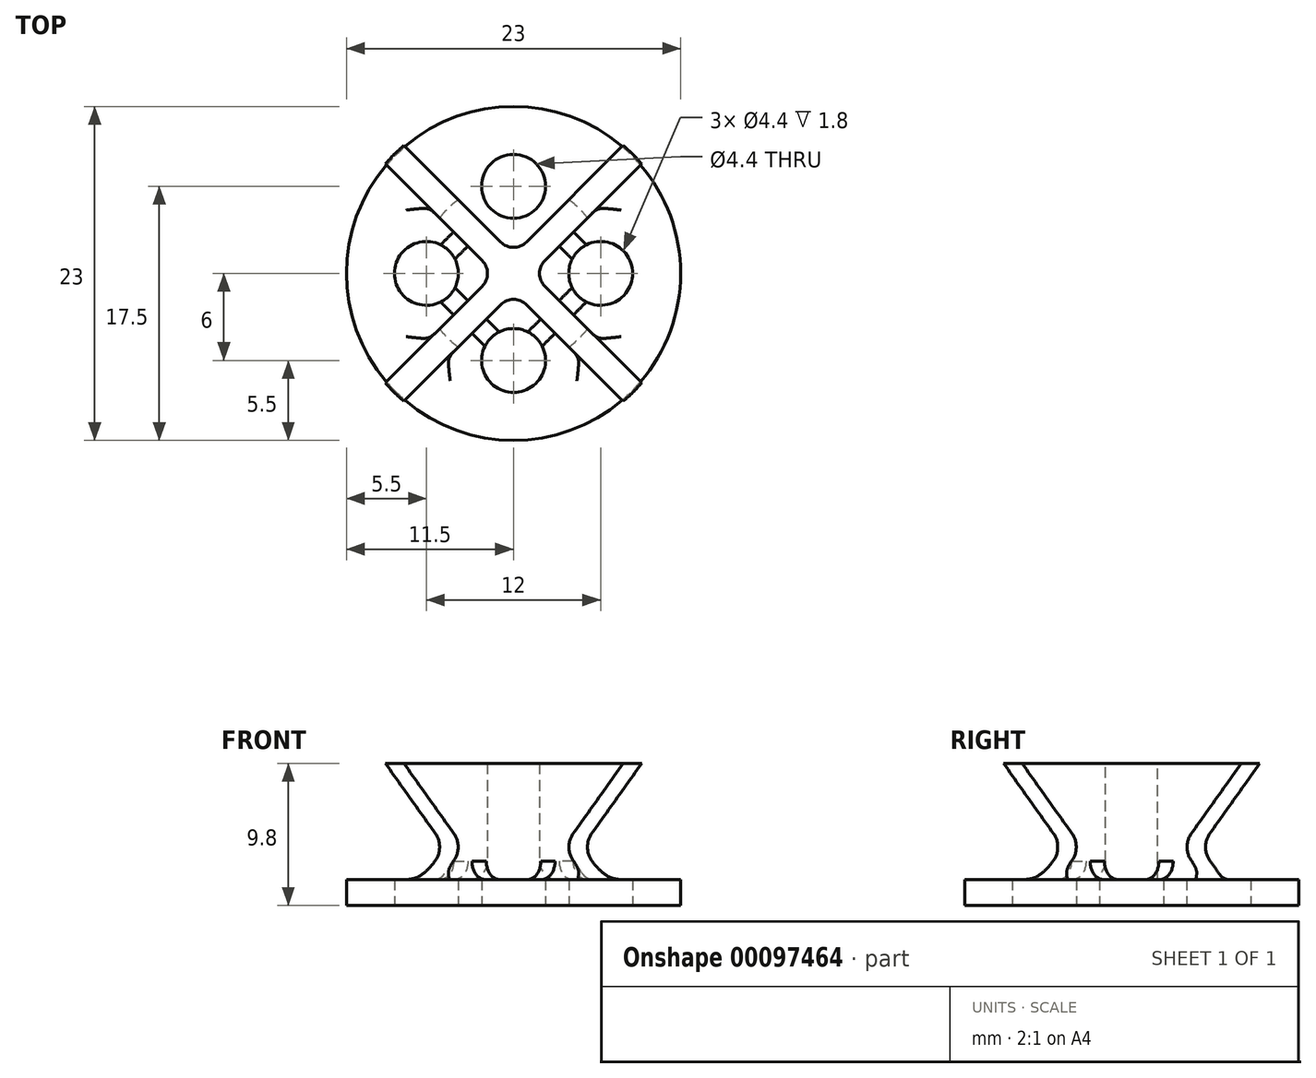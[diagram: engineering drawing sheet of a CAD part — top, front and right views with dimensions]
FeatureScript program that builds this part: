
annotation { "Feature Type Name" : "Feature", "Feature Type Description" : "" }
export const myFeature = defineFeature(function(context is Context, id is Id, definition is map)
    precondition{}
    {
        {
            assignVariable(context, id + "F0", {"name" : "thickness", "anyValue" : 1.8});
        }
        {
            var Q0;
            Q0=qCreatedBy(makeId("Top.planeOp"),FACE);
            var sketch = newSketch(context, id + "F1", { "sketchPlane" : qUnion([Q0])});
            skCircle(sketch, "E0", {"center": v(0, 0) * mm, "radius": 11.5 * mm});
            skSolve(sketch);
        }
        {
            var Q0;
            Q0=makeQuery(id+"F1.imprint","IMPRINT",FACE,{"disambiguationData":[TD([[makeQuery(id+"F1.imprint","IMPRINT",EDGE,{"derivedFrom":sQuery(id+"F1.wireOp",EDGE,"E0")}),1.0]])]});
            var sketch = newSketch(context, id + "F2", { "sketchPlane" : qUnion([Q0])});
            skCircle(sketch, "E1", {"center": v(0, 6) * mm, "radius": 2.2 * mm});
            skCircle(sketch, "E2.1.0", {"center": v(-6, 0) * mm, "radius": 2.2 * mm});
            skCircle(sketch, "E2.2.0", {"center": v(0, -6) * mm, "radius": 2.2 * mm});
            skCircle(sketch, "E2.3.0", {"center": v(6, 0) * mm, "radius": 2.2 * mm});
            skPoint(sketch, "E2.center", {"position": v(0, 0) * mm});
            skSolve(sketch);
        }
        {
            var Q0;
            Q0=qSketchRegion(id+"F1",true);
            extrude(context, id + "F3", {"entities" : qUnion([Q0]), "depth" : getVariable(context, 'thickness') * mm});
        }
        {
            var Q0;
            Q0=qSketchRegion(id+"F2",true);
            extrude(context, id + "F4", {"entities" : qUnion([Q0]), "operationType" : NewBodyOperationType.REMOVE, "depth" : 25 * mm});
        }
        {
            var Q0;
            Q0=makeQuery(id+"F3.opExtrude","CAP_FACE",FACE,{"disambiguationData":[OSD([sQuery(id+"F1.wireOp",EDGE,"E0")])],"isStart":false});
            var sketch = newSketch(context, id + "F5", { "sketchPlane" : qUnion([Q0])});
            skLineSegment(sketch, "E3.bottom", {"start": v(9.97, 11.24) * mm, "end": v(-11.24, -9.97) * mm});
            skLineSegment(sketch, "E3.top", {"start": v(11.24, 9.97) * mm, "end": v(-9.97, -11.24) * mm});
            skLineSegment(sketch, "E3.left", {"start": v(9.97, 11.24) * mm, "end": v(11.24, 9.97) * mm});
            skLineSegment(sketch, "E3.right", {"start": v(-11.24, -9.97) * mm, "end": v(-9.97, -11.24) * mm});
            skPoint(sketch, "E3.middle", {"position": v(0, 0) * mm});
            skLineSegment(sketch, "E4.1.0", {"start": v(11.24, -9.97) * mm, "end": v(-9.97, 11.24) * mm});
            skLineSegment(sketch, "E4.1.1", {"start": v(-9.97, 11.24) * mm, "end": v(-11.24, 9.97) * mm});
            skLineSegment(sketch, "E4.1.2", {"start": v(9.97, -11.24) * mm, "end": v(-11.24, 9.97) * mm});
            skLineSegment(sketch, "E4.1.3", {"start": v(11.24, -9.97) * mm, "end": v(9.97, -11.24) * mm});
            skLineSegment(sketch, "E4.anchor1", {"start": v(0, 0) * mm, "end": v(-9.97, -11.24) * mm, "construction": true});
            skLineSegment(sketch, "E4.anchor2", {"start": v(0, 0) * mm, "end": v(-11.24, 9.97) * mm, "construction": true});
            skSolve(sketch);
        }
        {
            var Q0;
            {var subQ0=sQuery(id+"F5.wireOp",EDGE,"E4.1.3");Q0=makeQuery(id+"F5.imprint","IMPRINT",FACE,{"disambiguationData":[TD([[makeQuery(id+"F5.imprint","IMPRINT",EDGE,{"derivedFrom":subQ0}),-1.0]])]});}
            var Q1;
            {var subQ0=sQuery(id+"F5.wireOp",EDGE,"E4.1.0");var subQ1=sQuery(id+"F5.wireOp",EDGE,"E3.top");var subQ2=makeQuery(id+"F5.imprint","INTERSECT",VERTEX,{"derivedFrom":[subQ1,subQ0]});Q1=makeQuery(id+"F5.imprint","IMPRINT",FACE,{"disambiguationData":[TD([[makeQuery(id+"F5.imprint","IMPRINT",EDGE,{"disambiguationData":[TD([[subQ2,-1.0]])],"derivedFrom":subQ1}),1.0]])]});}
            var Q2;
            {var subQ0=sQuery(id+"F5.wireOp",EDGE,"E3.right");Q2=makeQuery(id+"F5.imprint","IMPRINT",FACE,{"disambiguationData":[TD([[makeQuery(id+"F5.imprint","IMPRINT",EDGE,{"derivedFrom":subQ0}),1.0]])]});}
            var Q3;
            {var subQ0=sQuery(id+"F5.wireOp",EDGE,"E4.1.2");var subQ1=sQuery(id+"F5.wireOp",EDGE,"E3.bottom");var subQ2=makeQuery(id+"F5.imprint","INTERSECT",VERTEX,{"derivedFrom":[subQ1,subQ0]});Q3=makeQuery(id+"F5.imprint","IMPRINT",FACE,{"disambiguationData":[TD([[makeQuery(id+"F5.imprint","IMPRINT",EDGE,{"disambiguationData":[TD([[subQ2,-1.0]])],"derivedFrom":subQ1}),1.0]])]});}
            var Q4;
            {var subQ0=sQuery(id+"F5.wireOp",EDGE,"E4.1.0");var subQ1=sQuery(id+"F5.wireOp",EDGE,"E3.bottom");var subQ2=makeQuery(id+"F5.imprint","INTERSECT",VERTEX,{"derivedFrom":[subQ1,subQ0]});Q4=makeQuery(id+"F5.imprint","IMPRINT",FACE,{"disambiguationData":[TD([[makeQuery(id+"F5.imprint","IMPRINT",EDGE,{"disambiguationData":[TD([[subQ2,-1.0]])],"derivedFrom":subQ1}),1.0]])]});}
            var Q5;
            {var subQ0=sQuery(id+"F5.wireOp",EDGE,"E4.1.0");var subQ1=sQuery(id+"F5.wireOp",EDGE,"E3.bottom");var subQ2=makeQuery(id+"F5.imprint","INTERSECT",VERTEX,{"derivedFrom":[subQ1,subQ0]});Q5=makeQuery(id+"F5.imprint","IMPRINT",FACE,{"disambiguationData":[TD([[makeQuery(id+"F5.imprint","IMPRINT",EDGE,{"disambiguationData":[TD([[subQ2,-1.0]])],"derivedFrom":subQ1}),-1.0]])]});}
            var Q6;
            {var subQ0=sQuery(id+"F5.wireOp",EDGE,"E4.1.1");Q6=makeQuery(id+"F5.imprint","IMPRINT",FACE,{"disambiguationData":[TD([[makeQuery(id+"F5.imprint","IMPRINT",EDGE,{"derivedFrom":subQ0}),1.0]])]});}
            var Q7;
            {var subQ0=sQuery(id+"F5.wireOp",EDGE,"E4.1.0");var subQ1=sQuery(id+"F5.wireOp",EDGE,"E3.bottom");var subQ2=makeQuery(id+"F5.imprint","INTERSECT",VERTEX,{"derivedFrom":[subQ1,subQ0]});Q7=makeQuery(id+"F5.imprint","IMPRINT",FACE,{"disambiguationData":[TD([[makeQuery(id+"F5.imprint","IMPRINT",EDGE,{"disambiguationData":[TD([[subQ2,1.0]])],"derivedFrom":subQ1}),1.0]])]});}
            var Q8;
            {var subQ0=sQuery(id+"F5.wireOp",EDGE,"E3.left");Q8=makeQuery(id+"F5.imprint","IMPRINT",FACE,{"disambiguationData":[TD([[makeQuery(id+"F5.imprint","IMPRINT",EDGE,{"derivedFrom":subQ0}),-1.0]])]});}
            extrude(context, id + "F6", {"entities" : qUnion([Q0, Q1, Q2, Q3, Q4, Q5, Q6, Q7, Q8]), "operationType" : NewBodyOperationType.ADD, "depth" : 8 * mm});
        }
        {
            var Q0;
            {var subQ0=sQuery(id+"F5.wireOp",EDGE,"E4.1.2");Q0=makeQuery(id+"F6.opExtrude","SWEPT_FACE",FACE,{"disambiguationData":[OSD([subQ0]),TDD([makeQuery(id+"F5.imprint","IMPRINT",EDGE,{"disambiguationData":[TD([[makeQuery(id+"F5.imprint","INTERSECT",VERTEX,{"derivedFrom":[sQuery(id+"F5.wireOp",EDGE,"E4.1.1"),subQ0]}),1.0]])],"derivedFrom":subQ0})])]});}
            var Q1;
            {var subQ0=sQuery(id+"F5.wireOp",EDGE,"E4.1.0");Q1=makeQuery(id+"F6.opExtrude","SWEPT_FACE",FACE,{"disambiguationData":[OSD([subQ0]),TDD([makeQuery(id+"F5.imprint","IMPRINT",EDGE,{"disambiguationData":[TD([[makeQuery(id+"F5.imprint","INTERSECT",VERTEX,{"derivedFrom":[subQ0,sQuery(id+"F5.wireOp",EDGE,"E4.1.1")]}),1.0]])],"derivedFrom":subQ0})])]});}
            cPlane(context, id + "F7", {"entities" : qUnion([Q0, Q1]), "cplaneType" : CPlaneType.MID_PLANE, "offset" : 25 * mm, "width" : 150 * mm, "height" : 150 * mm});
        }
        {
            var Q0;
            Q0=qCreatedBy(makeId("Front.planeOp"),FACE);
            var sketch = newSketch(context, id + "F8", { "sketchPlane" : qUnion([Q0])});
            skLineSegment(sketch, "E5", {"start": v(0, 0) * mm, "end": v(0, 42) * mm});
            skSolve(sketch);
        }
        {
            var Q0;
            Q0=qCreatedBy(id+"F7.planeOp",FACE);
            var sketch = newSketch(context, id + "F9", { "sketchPlane" : qUnion([Q0])});
            skLineSegment(sketch, "E6", {"start": v(-26.4, 1.8) * mm, "end": v(-3.6, 1.8) * mm});
            skLineSegment(sketch, "E7", {"start": v(-3.6, 1.8) * mm, "end": v(-26.4, 24.6) * mm});
            skLineSegment(sketch, "E8", {"start": v(-26.4, 24.6) * mm, "end": v(-26.4, 1.8) * mm});
            skLineSegment(sketch, "E9", {"start": v(-5.84, 4.04) * mm, "end": v(-8.07, 1.8) * mm});
            skSolve(sketch);
        }
        {
            var Q0;
            {var subQ5=sQuery(id+"F9.wireOp",EDGE,"E8");Q0=makeQuery(id+"F9.imprint","IMPRINT",FACE,{"disambiguationData":[TD([[makeQuery(id+"F9.imprint","IMPRINT",EDGE,{"derivedFrom":subQ5}),1.0]])]});}
            var Q1;
            Q1=sQuery(id+"F8.wireOp",EDGE,"E5");
            revolve(context, id + "F10", {"operationType" : NewBodyOperationType.REMOVE, "entities" : qUnion([Q0]), "axis" : qUnion([Q1]), "revolveType" : RevolveType.FULL, "oppositeDirection" : true});
        }
        {
            var Q0;
            Q0=makeQuery(id+"F6.opExtrude","SWEPT_EDGE",EDGE,{"disambiguationData":[OSD([sQuery(id+"F5.wireOp",EDGE,"E3.top"),sQuery(id+"F5.wireOp",EDGE,"E4.1.2")])]});
            var Q1;
            {var subQ1=sQuery(id+"F5.wireOp",EDGE,"E3.right");var subQ2=sQuery(id+"F5.wireOp",EDGE,"E3.top");var subQ5=makeQuery(id+"F5.imprint","IMPRINT",EDGE,{"disambiguationData":[TD([[makeQuery(id+"F5.imprint","INTERSECT",VERTEX,{"derivedFrom":[subQ2,subQ1]}),1.0]])],"derivedFrom":subQ2});var subQ6=sQuery(id+"F5.wireOp",EDGE,"E4.1.2");var subQ7=makeQuery(id+"F5.imprint","INTERSECT",VERTEX,{"derivedFrom":[subQ2,subQ6]});var subQ8=makeQuery(id+"F5.imprint","IMPRINT",EDGE,{"disambiguationData":[TD([[subQ7,-1.0]])],"derivedFrom":subQ2});var subQ9=sQuery(id+"F5.wireOp",EDGE,"E4.1.3");Q1=makeQuery(id+"F6.boolean.opBoolean","SPLIT",EDGE,{"disambiguationData":[TD([makeQuery(id+"F6.opExtrude","SWEPT_FACE",FACE,{"disambiguationData":[OSD([subQ6]),TDD([makeQuery(id+"F5.imprint","IMPRINT",EDGE,{"disambiguationData":[TD([[makeQuery(id+"F5.imprint","INTERSECT",VERTEX,{"derivedFrom":[subQ6,subQ9]}),-1.0]])],"derivedFrom":subQ6}),makeQuery(id+"F5.imprint","IMPRINT",EDGE,{"disambiguationData":[TD([[subQ7,1.0]])],"derivedFrom":subQ6})])]})])],"derivedFrom":makeQuery(id+"F6.opExtrude","CAP_EDGE",EDGE,{"disambiguationData":[OSD([subQ2]),TDD([subQ8,subQ5])],"isStart":true})});}
            var Q2;
            {var subQ1=sQuery(id+"F5.wireOp",EDGE,"E3.right");var subQ2=sQuery(id+"F5.wireOp",EDGE,"E3.top");var subQ5=sQuery(id+"F5.wireOp",EDGE,"E4.1.2");var subQ6=makeQuery(id+"F5.imprint","INTERSECT",VERTEX,{"derivedFrom":[subQ2,subQ5]});var subQ7=sQuery(id+"F5.wireOp",EDGE,"E4.1.3");var subQ9=makeQuery(id+"F5.imprint","IMPRINT",EDGE,{"disambiguationData":[TD([[subQ6,1.0]])],"derivedFrom":subQ5});var subQ10=makeQuery(id+"F5.imprint","IMPRINT",EDGE,{"disambiguationData":[TD([[makeQuery(id+"F5.imprint","INTERSECT",VERTEX,{"derivedFrom":[subQ5,subQ7]}),-1.0]])],"derivedFrom":subQ5});Q2=makeQuery(id+"F6.boolean.opBoolean","SPLIT",EDGE,{"disambiguationData":[TD([makeQuery(id+"F6.opExtrude","SWEPT_FACE",FACE,{"disambiguationData":[OSD([subQ2]),TDD([makeQuery(id+"F5.imprint","IMPRINT",EDGE,{"disambiguationData":[TD([[subQ6,-1.0]])],"derivedFrom":subQ2}),makeQuery(id+"F5.imprint","IMPRINT",EDGE,{"disambiguationData":[TD([[makeQuery(id+"F5.imprint","INTERSECT",VERTEX,{"derivedFrom":[subQ2,subQ1]}),1.0]])],"derivedFrom":subQ2})])]})])],"derivedFrom":makeQuery(id+"F6.opExtrude","CAP_EDGE",EDGE,{"disambiguationData":[OSD([subQ5]),TDD([subQ10,subQ9])],"isStart":true})});}
            var Q3;
            Q3=makeQuery(id+"F6.opExtrude","SWEPT_EDGE",EDGE,{"disambiguationData":[OSD([sQuery(id+"F5.wireOp",EDGE,"E3.top"),sQuery(id+"F5.wireOp",EDGE,"E4.1.0")])]});
            var Q4;
            {var subQ1=sQuery(id+"F5.wireOp",EDGE,"E4.1.0");var subQ2=sQuery(id+"F5.wireOp",EDGE,"E3.top");var subQ3=makeQuery(id+"F5.imprint","INTERSECT",VERTEX,{"derivedFrom":[subQ2,subQ1]});var subQ6=sQuery(id+"F5.wireOp",EDGE,"E4.1.3");var subQ8=makeQuery(id+"F5.imprint","IMPRINT",EDGE,{"disambiguationData":[TD([[subQ3,1.0]])],"derivedFrom":subQ2});var subQ9=sQuery(id+"F5.wireOp",EDGE,"E3.left");var subQ10=makeQuery(id+"F5.imprint","IMPRINT",EDGE,{"disambiguationData":[TD([[makeQuery(id+"F5.imprint","INTERSECT",VERTEX,{"derivedFrom":[subQ2,subQ9]}),-1.0]])],"derivedFrom":subQ2});Q4=makeQuery(id+"F6.boolean.opBoolean","SPLIT",EDGE,{"disambiguationData":[TD([makeQuery(id+"F6.opExtrude","SWEPT_FACE",FACE,{"disambiguationData":[OSD([subQ1]),TDD([makeQuery(id+"F5.imprint","IMPRINT",EDGE,{"disambiguationData":[TD([[makeQuery(id+"F5.imprint","INTERSECT",VERTEX,{"derivedFrom":[subQ1,subQ6]}),-1.0]])],"derivedFrom":subQ1}),makeQuery(id+"F5.imprint","IMPRINT",EDGE,{"disambiguationData":[TD([[subQ3,1.0]])],"derivedFrom":subQ1})])]})])],"derivedFrom":makeQuery(id+"F6.opExtrude","CAP_EDGE",EDGE,{"disambiguationData":[OSD([subQ2]),TDD([subQ10,subQ8])],"isStart":true})});}
            var Q5;
            {var subQ1=sQuery(id+"F5.wireOp",EDGE,"E4.1.0");var subQ2=sQuery(id+"F5.wireOp",EDGE,"E3.top");var subQ3=makeQuery(id+"F5.imprint","INTERSECT",VERTEX,{"derivedFrom":[subQ2,subQ1]});var subQ6=makeQuery(id+"F5.imprint","IMPRINT",EDGE,{"disambiguationData":[TD([[subQ3,1.0]])],"derivedFrom":subQ1});var subQ7=sQuery(id+"F5.wireOp",EDGE,"E4.1.3");var subQ8=makeQuery(id+"F5.imprint","IMPRINT",EDGE,{"disambiguationData":[TD([[makeQuery(id+"F5.imprint","INTERSECT",VERTEX,{"derivedFrom":[subQ1,subQ7]}),-1.0]])],"derivedFrom":subQ1});var subQ10=sQuery(id+"F5.wireOp",EDGE,"E3.left");Q5=makeQuery(id+"F6.boolean.opBoolean","SPLIT",EDGE,{"disambiguationData":[TD([makeQuery(id+"F6.opExtrude","SWEPT_FACE",FACE,{"disambiguationData":[OSD([subQ2]),TDD([makeQuery(id+"F5.imprint","IMPRINT",EDGE,{"disambiguationData":[TD([[makeQuery(id+"F5.imprint","INTERSECT",VERTEX,{"derivedFrom":[subQ2,subQ10]}),-1.0]])],"derivedFrom":subQ2}),makeQuery(id+"F5.imprint","IMPRINT",EDGE,{"disambiguationData":[TD([[subQ3,1.0]])],"derivedFrom":subQ2})])]})])],"derivedFrom":makeQuery(id+"F6.opExtrude","CAP_EDGE",EDGE,{"disambiguationData":[OSD([subQ1]),TDD([subQ8,subQ6])],"isStart":true})});}
            var Q6;
            Q6=makeQuery(id+"F6.opExtrude","SWEPT_EDGE",EDGE,{"disambiguationData":[OSD([sQuery(id+"F5.wireOp",EDGE,"E3.bottom"),sQuery(id+"F5.wireOp",EDGE,"E4.1.2")])]});
            var Q7;
            {var subQ0=sQuery(id+"F5.wireOp",EDGE,"E3.right");var subQ1=sQuery(id+"F5.wireOp",EDGE,"E3.bottom");var subQ5=makeQuery(id+"F5.imprint","IMPRINT",EDGE,{"disambiguationData":[TD([[makeQuery(id+"F5.imprint","INTERSECT",VERTEX,{"derivedFrom":[subQ1,subQ0]}),1.0]])],"derivedFrom":subQ1});var subQ6=sQuery(id+"F5.wireOp",EDGE,"E4.1.2");var subQ7=makeQuery(id+"F5.imprint","INTERSECT",VERTEX,{"derivedFrom":[subQ1,subQ6]});var subQ8=makeQuery(id+"F5.imprint","IMPRINT",EDGE,{"disambiguationData":[TD([[subQ7,-1.0]])],"derivedFrom":subQ1});var subQ9=sQuery(id+"F5.wireOp",EDGE,"E4.1.1");Q7=makeQuery(id+"F6.boolean.opBoolean","SPLIT",EDGE,{"disambiguationData":[TD([makeQuery(id+"F6.opExtrude","SWEPT_FACE",FACE,{"disambiguationData":[OSD([subQ6]),TDD([makeQuery(id+"F5.imprint","IMPRINT",EDGE,{"disambiguationData":[TD([[subQ7,-1.0]])],"derivedFrom":subQ6}),makeQuery(id+"F5.imprint","IMPRINT",EDGE,{"disambiguationData":[TD([[makeQuery(id+"F5.imprint","INTERSECT",VERTEX,{"derivedFrom":[subQ9,subQ6]}),1.0]])],"derivedFrom":subQ6})])]})])],"derivedFrom":makeQuery(id+"F6.opExtrude","CAP_EDGE",EDGE,{"disambiguationData":[OSD([subQ1]),TDD([subQ8,subQ5])],"isStart":true})});}
            var Q8;
            {var subQ0=sQuery(id+"F5.wireOp",EDGE,"E3.right");var subQ1=sQuery(id+"F5.wireOp",EDGE,"E3.bottom");var subQ5=sQuery(id+"F5.wireOp",EDGE,"E4.1.2");var subQ6=makeQuery(id+"F5.imprint","INTERSECT",VERTEX,{"derivedFrom":[subQ1,subQ5]});var subQ7=sQuery(id+"F5.wireOp",EDGE,"E4.1.1");var subQ9=makeQuery(id+"F5.imprint","IMPRINT",EDGE,{"disambiguationData":[TD([[makeQuery(id+"F5.imprint","INTERSECT",VERTEX,{"derivedFrom":[subQ7,subQ5]}),1.0]])],"derivedFrom":subQ5});var subQ10=makeQuery(id+"F5.imprint","IMPRINT",EDGE,{"disambiguationData":[TD([[subQ6,-1.0]])],"derivedFrom":subQ5});Q8=makeQuery(id+"F6.boolean.opBoolean","SPLIT",EDGE,{"disambiguationData":[TD([makeQuery(id+"F6.opExtrude","SWEPT_FACE",FACE,{"disambiguationData":[OSD([subQ1]),TDD([makeQuery(id+"F5.imprint","IMPRINT",EDGE,{"disambiguationData":[TD([[subQ6,-1.0]])],"derivedFrom":subQ1}),makeQuery(id+"F5.imprint","IMPRINT",EDGE,{"disambiguationData":[TD([[makeQuery(id+"F5.imprint","INTERSECT",VERTEX,{"derivedFrom":[subQ1,subQ0]}),1.0]])],"derivedFrom":subQ1})])]})])],"derivedFrom":makeQuery(id+"F6.opExtrude","CAP_EDGE",EDGE,{"disambiguationData":[OSD([subQ5]),TDD([subQ10,subQ9])],"isStart":true})});}
            var Q9;
            {var subQ1=sQuery(id+"F5.wireOp",EDGE,"E4.1.1");var subQ2=sQuery(id+"F5.wireOp",EDGE,"E4.1.0");var subQ3=sQuery(id+"F5.wireOp",EDGE,"E3.left");var subQ4=sQuery(id+"F5.wireOp",EDGE,"E3.bottom");var subQ5=makeQuery(id+"F5.imprint","INTERSECT",VERTEX,{"derivedFrom":[subQ4,subQ2]});var subQ9=makeQuery(id+"F5.imprint","IMPRINT",EDGE,{"disambiguationData":[TD([[makeQuery(id+"F5.imprint","INTERSECT",VERTEX,{"derivedFrom":[subQ2,subQ1]}),1.0]])],"derivedFrom":subQ2});var subQ10=makeQuery(id+"F5.imprint","IMPRINT",EDGE,{"disambiguationData":[TD([[subQ5,-1.0]])],"derivedFrom":subQ2});Q9=makeQuery(id+"F6.boolean.opBoolean","SPLIT",EDGE,{"disambiguationData":[TD([makeQuery(id+"F6.opExtrude","SWEPT_FACE",FACE,{"disambiguationData":[OSD([subQ4]),TDD([makeQuery(id+"F5.imprint","IMPRINT",EDGE,{"disambiguationData":[TD([[makeQuery(id+"F5.imprint","INTERSECT",VERTEX,{"derivedFrom":[subQ4,subQ3]}),-1.0]])],"derivedFrom":subQ4}),makeQuery(id+"F5.imprint","IMPRINT",EDGE,{"disambiguationData":[TD([[subQ5,1.0]])],"derivedFrom":subQ4})])]})])],"derivedFrom":makeQuery(id+"F6.opExtrude","CAP_EDGE",EDGE,{"disambiguationData":[OSD([subQ2]),TDD([subQ10,subQ9])],"isStart":true})});}
            var Q10;
            {var subQ1=sQuery(id+"F5.wireOp",EDGE,"E4.1.1");var subQ2=sQuery(id+"F5.wireOp",EDGE,"E4.1.0");var subQ3=sQuery(id+"F5.wireOp",EDGE,"E3.left");var subQ4=sQuery(id+"F5.wireOp",EDGE,"E3.bottom");var subQ5=makeQuery(id+"F5.imprint","INTERSECT",VERTEX,{"derivedFrom":[subQ4,subQ2]});var subQ8=makeQuery(id+"F5.imprint","IMPRINT",EDGE,{"disambiguationData":[TD([[subQ5,1.0]])],"derivedFrom":subQ4});var subQ9=makeQuery(id+"F5.imprint","IMPRINT",EDGE,{"disambiguationData":[TD([[makeQuery(id+"F5.imprint","INTERSECT",VERTEX,{"derivedFrom":[subQ4,subQ3]}),-1.0]])],"derivedFrom":subQ4});Q10=makeQuery(id+"F6.boolean.opBoolean","SPLIT",EDGE,{"disambiguationData":[TD([makeQuery(id+"F6.opExtrude","SWEPT_FACE",FACE,{"disambiguationData":[OSD([subQ2]),TDD([makeQuery(id+"F5.imprint","IMPRINT",EDGE,{"disambiguationData":[TD([[subQ5,-1.0]])],"derivedFrom":subQ2}),makeQuery(id+"F5.imprint","IMPRINT",EDGE,{"disambiguationData":[TD([[makeQuery(id+"F5.imprint","INTERSECT",VERTEX,{"derivedFrom":[subQ2,subQ1]}),1.0]])],"derivedFrom":subQ2})])]})])],"derivedFrom":makeQuery(id+"F6.opExtrude","CAP_EDGE",EDGE,{"disambiguationData":[OSD([subQ4]),TDD([subQ9,subQ8])],"isStart":true})});}
            var Q11;
            Q11=makeQuery(id+"F6.opExtrude","SWEPT_EDGE",EDGE,{"disambiguationData":[OSD([sQuery(id+"F5.wireOp",EDGE,"E3.bottom"),sQuery(id+"F5.wireOp",EDGE,"E4.1.0")])]});
            var Q12;
            {var subQ0=sQuery(id+"F5.wireOp",EDGE,"E3.right");var subQ1=sQuery(id+"F5.wireOp",EDGE,"E3.bottom");var subQ4=sQuery(id+"F5.wireOp",EDGE,"E4.1.2");var subQ7=sQuery(id+"F9.wireOp",EDGE,"mvcvLoZS-Q1DX-C5zU-c2fG-Q9ep2RtqrYHX.bottom");var subQ8=sQuery(id+"F9.wireOp",EDGE,"mvcvLoZS-Q1DX-C5zU-c2fG-Q9ep2RtqrYHX.left");Q12=makeQuery(id+"F10.boolean.opBoolean","COPY",EDGE,{"disambiguationData":[TD([makeQuery(id+"F6.opExtrude","SWEPT_FACE",FACE,{"disambiguationData":[OSD([subQ1]),TDD([makeQuery(id+"F5.imprint","IMPRINT",EDGE,{"disambiguationData":[TD([[makeQuery(id+"F5.imprint","INTERSECT",VERTEX,{"derivedFrom":[subQ1,subQ4]}),-1.0]])],"derivedFrom":subQ1}),makeQuery(id+"F5.imprint","IMPRINT",EDGE,{"disambiguationData":[TD([[makeQuery(id+"F5.imprint","INTERSECT",VERTEX,{"derivedFrom":[subQ1,subQ0]}),1.0]])],"derivedFrom":subQ1})])]})])],"derivedFrom":makeQuery(id+"F10.opRevolve","SWEPT_EDGE",EDGE,{"disambiguationData":[OSD([subQ7,subQ8])]})});}
            var Q13;
            {var subQ0=sQuery(id+"F5.wireOp",EDGE,"E4.1.0");var subQ1=sQuery(id+"F5.wireOp",EDGE,"E3.top");var subQ4=sQuery(id+"F5.wireOp",EDGE,"E4.1.3");var subQ7=sQuery(id+"F9.wireOp",EDGE,"mvcvLoZS-Q1DX-C5zU-c2fG-Q9ep2RtqrYHX.bottom");var subQ8=sQuery(id+"F9.wireOp",EDGE,"mvcvLoZS-Q1DX-C5zU-c2fG-Q9ep2RtqrYHX.left");Q13=makeQuery(id+"F10.boolean.opBoolean","COPY",EDGE,{"disambiguationData":[TD([makeQuery(id+"F6.opExtrude","SWEPT_FACE",FACE,{"disambiguationData":[OSD([subQ0]),TDD([makeQuery(id+"F5.imprint","IMPRINT",EDGE,{"disambiguationData":[TD([[makeQuery(id+"F5.imprint","INTERSECT",VERTEX,{"derivedFrom":[subQ0,subQ4]}),-1.0]])],"derivedFrom":subQ0}),makeQuery(id+"F5.imprint","IMPRINT",EDGE,{"disambiguationData":[TD([[makeQuery(id+"F5.imprint","INTERSECT",VERTEX,{"derivedFrom":[subQ1,subQ0]}),1.0]])],"derivedFrom":subQ0})])]})])],"derivedFrom":makeQuery(id+"F10.opRevolve","SWEPT_EDGE",EDGE,{"disambiguationData":[OSD([subQ7,subQ8])]})});}
            var Q14;
            {var subQ0=sQuery(id+"F5.wireOp",EDGE,"E4.1.0");var subQ1=sQuery(id+"F5.wireOp",EDGE,"E3.bottom");var subQ4=sQuery(id+"F5.wireOp",EDGE,"E3.left");var subQ7=sQuery(id+"F9.wireOp",EDGE,"mvcvLoZS-Q1DX-C5zU-c2fG-Q9ep2RtqrYHX.bottom");var subQ8=sQuery(id+"F9.wireOp",EDGE,"mvcvLoZS-Q1DX-C5zU-c2fG-Q9ep2RtqrYHX.left");Q14=makeQuery(id+"F10.boolean.opBoolean","COPY",EDGE,{"disambiguationData":[TD([makeQuery(id+"F6.opExtrude","SWEPT_FACE",FACE,{"disambiguationData":[OSD([subQ1]),TDD([makeQuery(id+"F5.imprint","IMPRINT",EDGE,{"disambiguationData":[TD([[makeQuery(id+"F5.imprint","INTERSECT",VERTEX,{"derivedFrom":[subQ1,subQ4]}),-1.0]])],"derivedFrom":subQ1}),makeQuery(id+"F5.imprint","IMPRINT",EDGE,{"disambiguationData":[TD([[makeQuery(id+"F5.imprint","INTERSECT",VERTEX,{"derivedFrom":[subQ1,subQ0]}),1.0]])],"derivedFrom":subQ1})])]})])],"derivedFrom":makeQuery(id+"F10.opRevolve","SWEPT_EDGE",EDGE,{"disambiguationData":[OSD([subQ7,subQ8])]})});}
            var Q15;
            {var subQ0=sQuery(id+"F5.wireOp",EDGE,"E4.1.1");var subQ1=sQuery(id+"F5.wireOp",EDGE,"E4.1.0");var subQ4=sQuery(id+"F5.wireOp",EDGE,"E3.bottom");var subQ7=sQuery(id+"F9.wireOp",EDGE,"mvcvLoZS-Q1DX-C5zU-c2fG-Q9ep2RtqrYHX.bottom");var subQ8=sQuery(id+"F9.wireOp",EDGE,"mvcvLoZS-Q1DX-C5zU-c2fG-Q9ep2RtqrYHX.left");Q15=makeQuery(id+"F10.boolean.opBoolean","COPY",EDGE,{"disambiguationData":[TD([makeQuery(id+"F6.opExtrude","SWEPT_FACE",FACE,{"disambiguationData":[OSD([subQ1]),TDD([makeQuery(id+"F5.imprint","IMPRINT",EDGE,{"disambiguationData":[TD([[makeQuery(id+"F5.imprint","INTERSECT",VERTEX,{"derivedFrom":[subQ4,subQ1]}),-1.0]])],"derivedFrom":subQ1}),makeQuery(id+"F5.imprint","IMPRINT",EDGE,{"disambiguationData":[TD([[makeQuery(id+"F5.imprint","INTERSECT",VERTEX,{"derivedFrom":[subQ1,subQ0]}),1.0]])],"derivedFrom":subQ1})])]})])],"derivedFrom":makeQuery(id+"F10.opRevolve","SWEPT_EDGE",EDGE,{"disambiguationData":[OSD([subQ7,subQ8])]})});}
            var Q16;
            {var subQ0=sQuery(id+"F9.wireOp",EDGE,"E6");var subQ1=sQuery(id+"F5.wireOp",EDGE,"E4.1.0");var subQ2=sQuery(id+"F5.wireOp",EDGE,"E3.top");var subQ6=sQuery(id+"F5.wireOp",EDGE,"E4.1.3");var subQ9=sQuery(id+"F9.wireOp",EDGE,"E9");Q16=makeQuery(id+"F10.boolean.opBoolean","COPY",EDGE,{"disambiguationData":[TD([makeQuery(id+"F6.opExtrude","SWEPT_FACE",FACE,{"disambiguationData":[OSD([subQ1]),TDD([makeQuery(id+"F5.imprint","IMPRINT",EDGE,{"disambiguationData":[TD([[makeQuery(id+"F5.imprint","INTERSECT",VERTEX,{"derivedFrom":[subQ1,subQ6]}),-1.0]])],"derivedFrom":subQ1}),makeQuery(id+"F5.imprint","IMPRINT",EDGE,{"disambiguationData":[TD([[makeQuery(id+"F5.imprint","INTERSECT",VERTEX,{"derivedFrom":[subQ2,subQ1]}),1.0]])],"derivedFrom":subQ1})])]})])],"derivedFrom":makeQuery(id+"F10.opRevolve","SWEPT_EDGE",EDGE,{"disambiguationData":[OSD([subQ0,subQ9])]})});}
            var Q17;
            {var subQ0=sQuery(id+"F9.wireOp",EDGE,"E6");var subQ1=sQuery(id+"F5.wireOp",EDGE,"E4.1.0");var subQ6=sQuery(id+"F5.wireOp",EDGE,"E3.left");var subQ7=sQuery(id+"F9.wireOp",EDGE,"E9");var subQ8=sQuery(id+"F5.wireOp",EDGE,"E3.bottom");Q17=makeQuery(id+"F10.boolean.opBoolean","COPY",EDGE,{"disambiguationData":[TD([makeQuery(id+"F6.opExtrude","SWEPT_FACE",FACE,{"disambiguationData":[OSD([subQ8]),TDD([makeQuery(id+"F5.imprint","IMPRINT",EDGE,{"disambiguationData":[TD([[makeQuery(id+"F5.imprint","INTERSECT",VERTEX,{"derivedFrom":[subQ8,subQ6]}),-1.0]])],"derivedFrom":subQ8}),makeQuery(id+"F5.imprint","IMPRINT",EDGE,{"disambiguationData":[TD([[makeQuery(id+"F5.imprint","INTERSECT",VERTEX,{"derivedFrom":[subQ8,subQ1]}),1.0]])],"derivedFrom":subQ8})])]})])],"derivedFrom":makeQuery(id+"F10.opRevolve","SWEPT_EDGE",EDGE,{"disambiguationData":[OSD([subQ0,subQ7])]})});}
            var Q18;
            {var subQ0=sQuery(id+"F9.wireOp",EDGE,"E6");var subQ2=sQuery(id+"F5.wireOp",EDGE,"E4.1.1");var subQ6=sQuery(id+"F5.wireOp",EDGE,"E3.bottom");var subQ7=sQuery(id+"F5.wireOp",EDGE,"E4.1.0");var subQ9=sQuery(id+"F9.wireOp",EDGE,"E9");Q18=makeQuery(id+"F10.boolean.opBoolean","COPY",EDGE,{"disambiguationData":[TD([makeQuery(id+"F6.opExtrude","SWEPT_FACE",FACE,{"disambiguationData":[OSD([subQ7]),TDD([makeQuery(id+"F5.imprint","IMPRINT",EDGE,{"disambiguationData":[TD([[makeQuery(id+"F5.imprint","INTERSECT",VERTEX,{"derivedFrom":[subQ6,subQ7]}),-1.0]])],"derivedFrom":subQ7}),makeQuery(id+"F5.imprint","IMPRINT",EDGE,{"disambiguationData":[TD([[makeQuery(id+"F5.imprint","INTERSECT",VERTEX,{"derivedFrom":[subQ7,subQ2]}),1.0]])],"derivedFrom":subQ7})])]})])],"derivedFrom":makeQuery(id+"F10.opRevolve","SWEPT_EDGE",EDGE,{"disambiguationData":[OSD([subQ0,subQ9])]})});}
            var Q19;
            {var subQ0=sQuery(id+"F9.wireOp",EDGE,"E6");var subQ1=sQuery(id+"F5.wireOp",EDGE,"E3.right");var subQ6=sQuery(id+"F5.wireOp",EDGE,"E4.1.2");var subQ7=sQuery(id+"F5.wireOp",EDGE,"E3.bottom");var subQ9=sQuery(id+"F9.wireOp",EDGE,"E9");Q19=makeQuery(id+"F10.boolean.opBoolean","COPY",EDGE,{"disambiguationData":[TD([makeQuery(id+"F6.opExtrude","SWEPT_FACE",FACE,{"disambiguationData":[OSD([subQ7]),TDD([makeQuery(id+"F5.imprint","IMPRINT",EDGE,{"disambiguationData":[TD([[makeQuery(id+"F5.imprint","INTERSECT",VERTEX,{"derivedFrom":[subQ7,subQ6]}),-1.0]])],"derivedFrom":subQ7}),makeQuery(id+"F5.imprint","IMPRINT",EDGE,{"disambiguationData":[TD([[makeQuery(id+"F5.imprint","INTERSECT",VERTEX,{"derivedFrom":[subQ7,subQ1]}),1.0]])],"derivedFrom":subQ7})])]})])],"derivedFrom":makeQuery(id+"F10.opRevolve","SWEPT_EDGE",EDGE,{"disambiguationData":[OSD([subQ0,subQ9])]})});}
            var Q20;
            {var subQ0=sQuery(id+"F5.wireOp",EDGE,"E4.1.0");var subQ1=sQuery(id+"F5.wireOp",EDGE,"E3.top");var subQ4=sQuery(id+"F5.wireOp",EDGE,"E4.1.3");var subQ7=sQuery(id+"F9.wireOp",EDGE,"E7");var subQ8=sQuery(id+"F9.wireOp",EDGE,"E9");Q20=makeQuery(id+"F10.boolean.opBoolean","COPY",EDGE,{"disambiguationData":[TD([makeQuery(id+"F6.opExtrude","SWEPT_FACE",FACE,{"disambiguationData":[OSD([subQ0]),TDD([makeQuery(id+"F5.imprint","IMPRINT",EDGE,{"disambiguationData":[TD([[makeQuery(id+"F5.imprint","INTERSECT",VERTEX,{"derivedFrom":[subQ0,subQ4]}),-1.0]])],"derivedFrom":subQ0}),makeQuery(id+"F5.imprint","IMPRINT",EDGE,{"disambiguationData":[TD([[makeQuery(id+"F5.imprint","INTERSECT",VERTEX,{"derivedFrom":[subQ1,subQ0]}),1.0]])],"derivedFrom":subQ0})])]})])],"derivedFrom":makeQuery(id+"F10.opRevolve","SWEPT_EDGE",EDGE,{"disambiguationData":[OSD([subQ7,subQ8])]})});}
            var Q21;
            {var subQ0=sQuery(id+"F5.wireOp",EDGE,"E4.1.0");var subQ1=sQuery(id+"F5.wireOp",EDGE,"E3.bottom");var subQ4=sQuery(id+"F5.wireOp",EDGE,"E3.left");var subQ7=sQuery(id+"F9.wireOp",EDGE,"E7");var subQ8=sQuery(id+"F9.wireOp",EDGE,"E9");Q21=makeQuery(id+"F10.boolean.opBoolean","COPY",EDGE,{"disambiguationData":[TD([makeQuery(id+"F6.opExtrude","SWEPT_FACE",FACE,{"disambiguationData":[OSD([subQ1]),TDD([makeQuery(id+"F5.imprint","IMPRINT",EDGE,{"disambiguationData":[TD([[makeQuery(id+"F5.imprint","INTERSECT",VERTEX,{"derivedFrom":[subQ1,subQ4]}),-1.0]])],"derivedFrom":subQ1}),makeQuery(id+"F5.imprint","IMPRINT",EDGE,{"disambiguationData":[TD([[makeQuery(id+"F5.imprint","INTERSECT",VERTEX,{"derivedFrom":[subQ1,subQ0]}),1.0]])],"derivedFrom":subQ1})])]})])],"derivedFrom":makeQuery(id+"F10.opRevolve","SWEPT_EDGE",EDGE,{"disambiguationData":[OSD([subQ7,subQ8])]})});}
            var Q22;
            {var subQ0=sQuery(id+"F5.wireOp",EDGE,"E4.1.1");var subQ1=sQuery(id+"F5.wireOp",EDGE,"E4.1.0");var subQ4=sQuery(id+"F5.wireOp",EDGE,"E3.bottom");var subQ7=sQuery(id+"F9.wireOp",EDGE,"E7");var subQ8=sQuery(id+"F9.wireOp",EDGE,"E9");Q22=makeQuery(id+"F10.boolean.opBoolean","COPY",EDGE,{"disambiguationData":[TD([makeQuery(id+"F6.opExtrude","SWEPT_FACE",FACE,{"disambiguationData":[OSD([subQ1]),TDD([makeQuery(id+"F5.imprint","IMPRINT",EDGE,{"disambiguationData":[TD([[makeQuery(id+"F5.imprint","INTERSECT",VERTEX,{"derivedFrom":[subQ4,subQ1]}),-1.0]])],"derivedFrom":subQ1}),makeQuery(id+"F5.imprint","IMPRINT",EDGE,{"disambiguationData":[TD([[makeQuery(id+"F5.imprint","INTERSECT",VERTEX,{"derivedFrom":[subQ1,subQ0]}),1.0]])],"derivedFrom":subQ1})])]})])],"derivedFrom":makeQuery(id+"F10.opRevolve","SWEPT_EDGE",EDGE,{"disambiguationData":[OSD([subQ7,subQ8])]})});}
            var Q23;
            {var subQ0=sQuery(id+"F5.wireOp",EDGE,"E3.right");var subQ1=sQuery(id+"F5.wireOp",EDGE,"E3.bottom");var subQ4=sQuery(id+"F5.wireOp",EDGE,"E4.1.2");var subQ5=sQuery(id+"F9.wireOp",EDGE,"E7");var subQ6=sQuery(id+"F9.wireOp",EDGE,"E9");Q23=makeQuery(id+"F10.boolean.opBoolean","COPY",EDGE,{"disambiguationData":[TD([makeQuery(id+"F6.opExtrude","SWEPT_FACE",FACE,{"disambiguationData":[OSD([subQ1]),TDD([makeQuery(id+"F5.imprint","IMPRINT",EDGE,{"disambiguationData":[TD([[makeQuery(id+"F5.imprint","INTERSECT",VERTEX,{"derivedFrom":[subQ1,subQ4]}),-1.0]])],"derivedFrom":subQ1}),makeQuery(id+"F5.imprint","IMPRINT",EDGE,{"disambiguationData":[TD([[makeQuery(id+"F5.imprint","INTERSECT",VERTEX,{"derivedFrom":[subQ1,subQ0]}),1.0]])],"derivedFrom":subQ1})])]})])],"derivedFrom":makeQuery(id+"F10.opRevolve","SWEPT_EDGE",EDGE,{"disambiguationData":[OSD([subQ5,subQ6])]})});}
            fillet(context, id + "F11", {"entities" : qUnion([Q0, Q1, Q2, Q3, Q4, Q5, Q6, Q7, Q8, Q9, Q10, Q11, Q12, Q13, Q14, Q15, Q16, Q17, Q18, Q19, Q20, Q21, Q22, Q23]), "radius" : 1.26 * mm, "tangentPropagation" : true, "allowEdgeOverflow" : false});
        }
        {
            var Q0;
            {var subQ3=sQuery(id+"F1.wireOp",EDGE,"E0");var subQ15=makeQuery(id+"F3.opExtrude","CAP_FACE",FACE,{"disambiguationData":[OSD([subQ3])],"isStart":false});Q0=makeQuery(id+"F10.boolean.opBoolean","MERGE",FACE,{"derivedFrom":[makeQuery(id+"F6.boolean.opBoolean","SPLIT",FACE,{"disambiguationData":[TD([makeQuery(id+"F4.boolean.opBoolean","COPY",FACE,{"derivedFrom":makeQuery(id+"F4.opExtrude","SWEPT_FACE",FACE,{"disambiguationData":[OSD([sQuery(id+"F2.wireOp",EDGE,"E1")])]})})])],"derivedFrom":subQ15}),makeQuery(id+"F6.boolean.opBoolean","SPLIT",FACE,{"disambiguationData":[TD([makeQuery(id+"F4.boolean.opBoolean","COPY",FACE,{"derivedFrom":makeQuery(id+"F4.opExtrude","SWEPT_FACE",FACE,{"disambiguationData":[OSD([sQuery(id+"F2.wireOp",EDGE,"E2.1.0")])]})})])],"derivedFrom":subQ15}),makeQuery(id+"F6.boolean.opBoolean","SPLIT",FACE,{"disambiguationData":[TD([makeQuery(id+"F4.boolean.opBoolean","COPY",FACE,{"derivedFrom":makeQuery(id+"F4.opExtrude","SWEPT_FACE",FACE,{"disambiguationData":[OSD([sQuery(id+"F2.wireOp",EDGE,"E2.2.0")])]})})])],"derivedFrom":subQ15}),makeQuery(id+"F6.boolean.opBoolean","SPLIT",FACE,{"disambiguationData":[TD([makeQuery(id+"F4.boolean.opBoolean","COPY",FACE,{"derivedFrom":makeQuery(id+"F4.opExtrude","SWEPT_FACE",FACE,{"disambiguationData":[OSD([sQuery(id+"F2.wireOp",EDGE,"E2.3.0")])]})})])],"derivedFrom":subQ15}),makeQuery(id+"F10.opRevolve","SWEPT_FACE",FACE,{"disambiguationData":[OSD([sQuery(id+"F9.wireOp",EDGE,"E6")])]})]});}
            var sketch = newSketch(context, id + "F12", { "sketchPlane" : qUnion([Q0])});
            skCircle(sketch, "E10", {"center": v(0, 6) * mm, "radius": 2 * mm});
            skCircle(sketch, "E11.1.0", {"center": v(-6, 0) * mm, "radius": 2 * mm});
            skCircle(sketch, "E11.2.0", {"center": v(0, -6) * mm, "radius": 2 * mm});
            skCircle(sketch, "E11.3.0", {"center": v(6, 0) * mm, "radius": 2 * mm});
            skPoint(sketch, "E11.center", {"position": v(0, 0) * mm});
            skSolve(sketch);
        }
        {
            var Q0;
            Q0=qSketchRegion(id+"F12",true);
            extrude(context, id + "F13", {"entities" : qUnion([Q0]), "operationType" : NewBodyOperationType.REMOVE, "oppositeDirection" : true, "depth" : 0.5 * mm});
        }
    });
